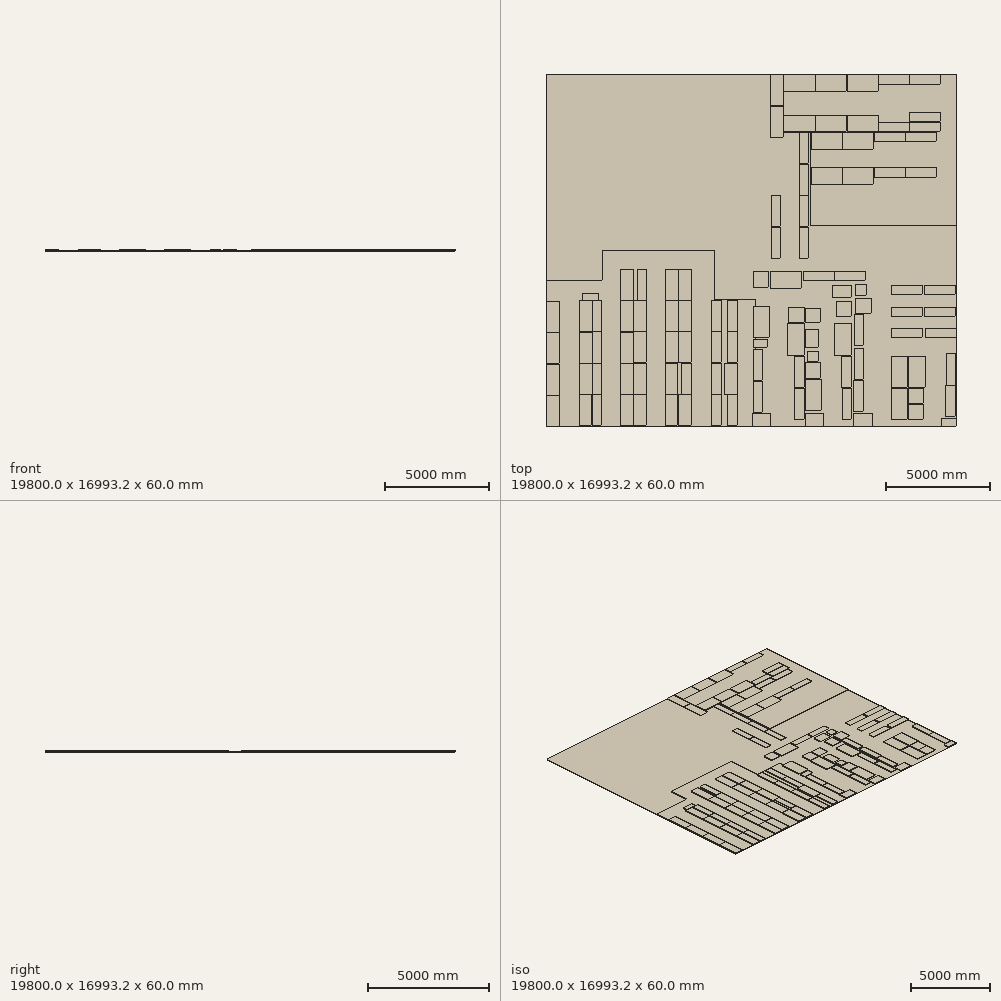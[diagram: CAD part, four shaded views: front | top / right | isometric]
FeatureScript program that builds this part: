
annotation { "Feature Type Name" : "Feature", "Feature Type Description" : "" }
export const myFeature = defineFeature(function(context is Context, id is Id, definition is map)
    precondition{}
    {
        {
            var Q0;
            Q0=qCreatedBy(makeId("Top.planeOp"),FACE);
            var sketch = newSketch(context, id + "F0", { "sketchPlane" : qUnion([Q0])});
            skLineSegment(sketch, "E0.bottom", {"start": v(9900, -8495) * mm, "end": v(-9900, -8495) * mm});
            skLineSegment(sketch, "E0.top", {"start": v(9900, 8495) * mm, "end": v(-9900, 8495) * mm});
            skLineSegment(sketch, "E0.left", {"start": v(9900, -8495) * mm, "end": v(9900, 8495) * mm});
            skLineSegment(sketch, "E0.right", {"start": v(-9900, -8495) * mm, "end": v(-9900, 8495) * mm});
            skPoint(sketch, "E0.middle", {"position": v(0, 0) * mm});
            skSolve(sketch);
        }
        {
            var Q0;
            Q0 = qSketchRegion(id + "F0", true);
            extrude(context, id + "F1", {"entities" : qUnion([Q0]), "depth" : 10 * mm});
        }
        {
            var Q0;
            Q0=makeQuery(id+"F1.opExtrude","CAP_FACE",FACE,{"disambiguationData":[OSD([sQuery(id+"F0.wireOp",EDGE,"E0.bottom"),sQuery(id+"F0.wireOp",EDGE,"E0.top"),sQuery(id+"F0.wireOp",EDGE,"E0.left"),sQuery(id+"F0.wireOp",EDGE,"E0.right")])],"isStart":false});
            var sketch = newSketch(context, id + "F2", { "sketchPlane" : qUnion([Q0])});
            skLineSegment(sketch, "E1", {"start": v(-9900, -8495) * mm, "end": v(-9900, -1435) * mm});
            skLineSegment(sketch, "E2", {"start": v(-9900, -1435) * mm, "end": v(-7200, -1435) * mm});
            skLineSegment(sketch, "E3", {"start": v(-7200, -1435) * mm, "end": v(-7200, -5) * mm});
            skLineSegment(sketch, "E4", {"start": v(-7200, -5) * mm, "end": v(-1800, -5) * mm});
            skLineSegment(sketch, "E5", {"start": v(-1800, -5) * mm, "end": v(-1800, -2355) * mm});
            skLineSegment(sketch, "E6", {"start": v(-1800, -2355) * mm, "end": v(200, -2355) * mm});
            skLineSegment(sketch, "E7", {"start": v(200, -2355) * mm, "end": v(200, -8495) * mm});
            skLineSegment(sketch, "E8", {"start": v(200, -8495) * mm, "end": v(-9900, -8495) * mm});
            skLineSegment(sketch, "E9", {"start": v(9900, 1195) * mm, "end": v(9900, 8495) * mm});
            skLineSegment(sketch, "E10", {"start": v(9900, 8495) * mm, "end": v(1550, 8495) * mm});
            skLineSegment(sketch, "E11", {"start": v(1550, 8495) * mm, "end": v(1550, 5715) * mm});
            skLineSegment(sketch, "E12", {"start": v(1550, 5715) * mm, "end": v(2850, 5715) * mm});
            skLineSegment(sketch, "E13", {"start": v(2850, 5715) * mm, "end": v(2850, 1195) * mm});
            skLineSegment(sketch, "E14", {"start": v(2850, 1195) * mm, "end": v(9900, 1195) * mm});
            skLineSegment(sketch, "E15.left", {"start": v(3458.32, 469.72) * mm, "end": v(3008.32, 469.72) * mm});
            skPoint(sketch, "E15.middle", {"position": v(3233.32, -280.28) * mm});
            skLineSegment(sketch, "E16.left", {"start": v(4716.05, -36.44) * mm, "end": v(4096.05, -36.44) * mm});
            skPoint(sketch, "E16.middle", {"position": v(4406.05, -786.44) * mm});
            skSolve(sketch);
        }
        {
            var Q0;
            Q0 = qSketchRegion(id + "F2", true);
            extrude(context, id + "F3", {"entities" : qUnion([Q0]), "operationType" : NewBodyOperationType.ADD, "depth" : 25 * mm});
        }
        {
            var Q0;
            Q0=makeQuery(id+"F3.opExtrude","CAP_FACE",FACE,{"disambiguationData":[OSD([sQuery(id+"F2.wireOp",EDGE,"E1"),sQuery(id+"F2.wireOp",EDGE,"E2"),sQuery(id+"F2.wireOp",EDGE,"E3"),sQuery(id+"F2.wireOp",EDGE,"E4"),sQuery(id+"F2.wireOp",EDGE,"E5"),sQuery(id+"F2.wireOp",EDGE,"E6"),sQuery(id+"F2.wireOp",EDGE,"E7"),sQuery(id+"F2.wireOp",EDGE,"E8")])],"isStart":false});
            var sketch = newSketch(context, id + "F4", { "sketchPlane" : qUnion([Q0])});
            skLineSegment(sketch, "E17.bottom", {"start": v(-9900, -8495) * mm, "end": v(-9900, -6995) * mm});
            skLineSegment(sketch, "E17.top", {"start": v(-9280, -8495) * mm, "end": v(-9280, -6995) * mm});
            skLineSegment(sketch, "E17.left", {"start": v(-9900, -8495) * mm, "end": v(-9280, -8495) * mm});
            skLineSegment(sketch, "E17.right", {"start": v(-9900, -6995) * mm, "end": v(-9280, -6995) * mm});
            skPoint(sketch, "E17.middle", {"position": v(-9590, -7745) * mm});
            skLineSegment(sketch, "E18.bottom", {"start": v(-9892.84, -6987.42) * mm, "end": v(-9892.84, -5487.42) * mm});
            skLineSegment(sketch, "E18.top", {"start": v(-9272.84, -6987.42) * mm, "end": v(-9272.84, -5487.42) * mm});
            skLineSegment(sketch, "E18.left", {"start": v(-9892.84, -6987.42) * mm, "end": v(-9272.84, -6987.42) * mm});
            skLineSegment(sketch, "E18.right", {"start": v(-9892.84, -5487.42) * mm, "end": v(-9272.84, -5487.42) * mm});
            skPoint(sketch, "E18.middle", {"position": v(-9582.84, -6237.42) * mm});
            skLineSegment(sketch, "E19.bottom", {"start": v(-9892.84, -5474.56) * mm, "end": v(-9892.84, -3974.56) * mm});
            skLineSegment(sketch, "E19.top", {"start": v(-9272.84, -5474.56) * mm, "end": v(-9272.84, -3974.56) * mm});
            skLineSegment(sketch, "E19.left", {"start": v(-9892.84, -5474.56) * mm, "end": v(-9272.84, -5474.56) * mm});
            skLineSegment(sketch, "E19.right", {"start": v(-9892.84, -3974.56) * mm, "end": v(-9272.84, -3974.56) * mm});
            skPoint(sketch, "E19.middle", {"position": v(-9582.84, -4724.56) * mm});
            skLineSegment(sketch, "E20.bottom", {"start": v(-9892.84, -3964.29) * mm, "end": v(-9892.84, -2464.29) * mm});
            skLineSegment(sketch, "E20.top", {"start": v(-9272.84, -3964.29) * mm, "end": v(-9272.84, -2464.29) * mm});
            skLineSegment(sketch, "E20.left", {"start": v(-9892.84, -3964.29) * mm, "end": v(-9272.84, -3964.29) * mm});
            skLineSegment(sketch, "E20.right", {"start": v(-9892.84, -2464.29) * mm, "end": v(-9272.84, -2464.29) * mm});
            skPoint(sketch, "E20.middle", {"position": v(-9582.84, -3214.29) * mm});
            skLineSegment(sketch, "E21.bottom", {"start": v(-8329.6, -8467.89) * mm, "end": v(-8329.6, -6967.89) * mm});
            skLineSegment(sketch, "E21.top", {"start": v(-7709.6, -8467.89) * mm, "end": v(-7709.6, -6967.89) * mm});
            skLineSegment(sketch, "E21.left", {"start": v(-8329.6, -8467.89) * mm, "end": v(-7709.6, -8467.89) * mm});
            skLineSegment(sketch, "E21.right", {"start": v(-8329.6, -6967.89) * mm, "end": v(-7709.6, -6967.89) * mm});
            skPoint(sketch, "E21.middle", {"position": v(-8019.6, -7717.89) * mm});
            skLineSegment(sketch, "E22.bottom", {"start": v(-8322.44, -6960.31) * mm, "end": v(-8322.44, -5460.31) * mm});
            skLineSegment(sketch, "E22.top", {"start": v(-7702.44, -6960.31) * mm, "end": v(-7702.44, -5460.31) * mm});
            skLineSegment(sketch, "E22.left", {"start": v(-8322.44, -6960.31) * mm, "end": v(-7702.44, -6960.31) * mm});
            skLineSegment(sketch, "E22.right", {"start": v(-8322.44, -5460.31) * mm, "end": v(-7702.44, -5460.31) * mm});
            skPoint(sketch, "E22.middle", {"position": v(-8012.44, -6210.31) * mm});
            skLineSegment(sketch, "E23.bottom", {"start": v(-8322.44, -5447.45) * mm, "end": v(-8322.44, -3947.45) * mm});
            skLineSegment(sketch, "E23.top", {"start": v(-7702.44, -5447.45) * mm, "end": v(-7702.44, -3947.45) * mm});
            skLineSegment(sketch, "E23.left", {"start": v(-8322.44, -5447.45) * mm, "end": v(-7702.44, -5447.45) * mm});
            skLineSegment(sketch, "E23.right", {"start": v(-8322.44, -3947.45) * mm, "end": v(-7702.44, -3947.45) * mm});
            skPoint(sketch, "E23.middle", {"position": v(-8012.44, -4697.45) * mm});
            skLineSegment(sketch, "E24.bottom", {"start": v(-8322.44, -3937.18) * mm, "end": v(-8322.44, -2437.18) * mm});
            skLineSegment(sketch, "E24.top", {"start": v(-7702.44, -3937.18) * mm, "end": v(-7702.44, -2437.18) * mm});
            skLineSegment(sketch, "E24.left", {"start": v(-8322.44, -3937.18) * mm, "end": v(-7702.44, -3937.18) * mm});
            skLineSegment(sketch, "E24.right", {"start": v(-8322.44, -2437.18) * mm, "end": v(-7702.44, -2437.18) * mm});
            skPoint(sketch, "E24.middle", {"position": v(-8012.44, -3187.18) * mm});
            skLineSegment(sketch, "E25.bottom", {"start": v(-7690, -8467.89) * mm, "end": v(-7690, -6967.89) * mm});
            skLineSegment(sketch, "E25.top", {"start": v(-7240, -8467.89) * mm, "end": v(-7240, -6967.89) * mm});
            skLineSegment(sketch, "E25.left", {"start": v(-7690, -8467.89) * mm, "end": v(-7240, -8467.89) * mm});
            skLineSegment(sketch, "E25.right", {"start": v(-7690, -6967.89) * mm, "end": v(-7240, -6967.89) * mm});
            skPoint(sketch, "E25.middle", {"position": v(-7465, -7717.89) * mm});
            skLineSegment(sketch, "E26.bottom", {"start": v(-7690, -6949.05) * mm, "end": v(-7690, -5449.05) * mm});
            skLineSegment(sketch, "E26.top", {"start": v(-7240, -6949.05) * mm, "end": v(-7240, -5449.05) * mm});
            skLineSegment(sketch, "E26.left", {"start": v(-7690, -6949.05) * mm, "end": v(-7240, -6949.05) * mm});
            skLineSegment(sketch, "E26.right", {"start": v(-7690, -5449.05) * mm, "end": v(-7240, -5449.05) * mm});
            skPoint(sketch, "E26.middle", {"position": v(-7465, -6199.05) * mm});
            skLineSegment(sketch, "E27.bottom", {"start": v(-7690, -5437.57) * mm, "end": v(-7690, -3937.57) * mm});
            skLineSegment(sketch, "E27.top", {"start": v(-7240, -5437.57) * mm, "end": v(-7240, -3937.57) * mm});
            skLineSegment(sketch, "E27.left", {"start": v(-7690, -5437.57) * mm, "end": v(-7240, -5437.57) * mm});
            skLineSegment(sketch, "E27.right", {"start": v(-7690, -3937.57) * mm, "end": v(-7240, -3937.57) * mm});
            skPoint(sketch, "E27.middle", {"position": v(-7465, -4687.57) * mm});
            skLineSegment(sketch, "E28.bottom", {"start": v(-7690, -3928.07) * mm, "end": v(-7690, -2428.07) * mm});
            skLineSegment(sketch, "E28.top", {"start": v(-7240, -3928.07) * mm, "end": v(-7240, -2428.07) * mm});
            skLineSegment(sketch, "E28.left", {"start": v(-7690, -3928.07) * mm, "end": v(-7240, -3928.07) * mm});
            skLineSegment(sketch, "E28.right", {"start": v(-7690, -2428.07) * mm, "end": v(-7240, -2428.07) * mm});
            skPoint(sketch, "E28.middle", {"position": v(-7465, -3178.07) * mm});
            skLineSegment(sketch, "E29.bottom", {"start": v(-8177.13, -2054.5) * mm, "end": v(-7388.6, -2054.5) * mm});
            skLineSegment(sketch, "E29.top", {"start": v(-8177.13, -2400.4) * mm, "end": v(-7388.6, -2400.4) * mm});
            skLineSegment(sketch, "E29.left", {"start": v(-8177.13, -2054.5) * mm, "end": v(-8177.13, -2400.4) * mm});
            skLineSegment(sketch, "E29.right", {"start": v(-7388.6, -2054.5) * mm, "end": v(-7388.6, -2400.4) * mm});
            skLineSegment(sketch, "E30.bottom", {"start": v(-6340, -8467.89) * mm, "end": v(-6340, -6967.89) * mm});
            skLineSegment(sketch, "E30.top", {"start": v(-5720, -8467.89) * mm, "end": v(-5720, -6967.89) * mm});
            skLineSegment(sketch, "E30.left", {"start": v(-6340, -8467.89) * mm, "end": v(-5720, -8467.89) * mm});
            skLineSegment(sketch, "E30.right", {"start": v(-6340, -6967.89) * mm, "end": v(-5720, -6967.89) * mm});
            skPoint(sketch, "E30.middle", {"position": v(-6030, -7717.89) * mm});
            skLineSegment(sketch, "E31.bottom", {"start": v(-6340, -6949.05) * mm, "end": v(-6340, -5449.05) * mm});
            skLineSegment(sketch, "E31.top", {"start": v(-5720, -6949.05) * mm, "end": v(-5720, -5449.05) * mm});
            skLineSegment(sketch, "E31.left", {"start": v(-6340, -6949.05) * mm, "end": v(-5720, -6949.05) * mm});
            skLineSegment(sketch, "E31.right", {"start": v(-6340, -5449.05) * mm, "end": v(-5720, -5449.05) * mm});
            skPoint(sketch, "E31.middle", {"position": v(-6030, -6199.05) * mm});
            skLineSegment(sketch, "E32.bottom", {"start": v(-6332.83, -5441.47) * mm, "end": v(-6332.83, -3941.47) * mm});
            skLineSegment(sketch, "E32.top", {"start": v(-5712.83, -5441.47) * mm, "end": v(-5712.83, -3941.47) * mm});
            skLineSegment(sketch, "E32.left", {"start": v(-6332.83, -5441.47) * mm, "end": v(-5712.83, -5441.47) * mm});
            skLineSegment(sketch, "E32.right", {"start": v(-6332.83, -3941.47) * mm, "end": v(-5712.83, -3941.47) * mm});
            skPoint(sketch, "E32.middle", {"position": v(-6022.83, -4691.47) * mm});
            skLineSegment(sketch, "E33.bottom", {"start": v(-6332.83, -3928.6) * mm, "end": v(-6332.83, -2428.6) * mm});
            skLineSegment(sketch, "E33.top", {"start": v(-5712.83, -3928.6) * mm, "end": v(-5712.83, -2428.6) * mm});
            skLineSegment(sketch, "E33.left", {"start": v(-6332.83, -3928.6) * mm, "end": v(-5712.83, -3928.6) * mm});
            skLineSegment(sketch, "E33.right", {"start": v(-6332.83, -2428.6) * mm, "end": v(-5712.83, -2428.6) * mm});
            skPoint(sketch, "E33.middle", {"position": v(-6022.83, -3178.6) * mm});
            skLineSegment(sketch, "E34.bottom", {"start": v(-6332.83, -2418.34) * mm, "end": v(-6332.83, -918.34) * mm});
            skLineSegment(sketch, "E34.top", {"start": v(-5712.83, -2418.34) * mm, "end": v(-5712.83, -918.34) * mm});
            skLineSegment(sketch, "E34.left", {"start": v(-6332.83, -2418.34) * mm, "end": v(-5712.83, -2418.34) * mm});
            skLineSegment(sketch, "E34.right", {"start": v(-6332.83, -918.34) * mm, "end": v(-5712.83, -918.34) * mm});
            skPoint(sketch, "E34.middle", {"position": v(-6022.83, -1668.34) * mm});
            skLineSegment(sketch, "E35.bottom", {"start": v(-5694.35, -8456.4) * mm, "end": v(-5694.35, -6956.4) * mm});
            skLineSegment(sketch, "E35.top", {"start": v(-5074.35, -8456.4) * mm, "end": v(-5074.35, -6956.4) * mm});
            skLineSegment(sketch, "E35.left", {"start": v(-5694.35, -8456.4) * mm, "end": v(-5074.35, -8456.4) * mm});
            skLineSegment(sketch, "E35.right", {"start": v(-5694.35, -6956.4) * mm, "end": v(-5074.35, -6956.4) * mm});
            skPoint(sketch, "E35.middle", {"position": v(-5384.35, -7706.4) * mm});
            skLineSegment(sketch, "E36.bottom", {"start": v(-5694.35, -6937.55) * mm, "end": v(-5694.35, -5437.55) * mm});
            skLineSegment(sketch, "E36.top", {"start": v(-5074.35, -6937.55) * mm, "end": v(-5074.35, -5437.55) * mm});
            skLineSegment(sketch, "E36.left", {"start": v(-5694.35, -6937.55) * mm, "end": v(-5074.35, -6937.55) * mm});
            skLineSegment(sketch, "E36.right", {"start": v(-5694.35, -5437.55) * mm, "end": v(-5074.35, -5437.55) * mm});
            skPoint(sketch, "E36.middle", {"position": v(-5384.35, -6187.55) * mm});
            skLineSegment(sketch, "E37.bottom", {"start": v(-5687.2, -5429.97) * mm, "end": v(-5687.2, -3929.97) * mm});
            skLineSegment(sketch, "E37.top", {"start": v(-5067.2, -5429.97) * mm, "end": v(-5067.2, -3929.97) * mm});
            skLineSegment(sketch, "E37.left", {"start": v(-5687.2, -5429.97) * mm, "end": v(-5067.2, -5429.97) * mm});
            skLineSegment(sketch, "E37.right", {"start": v(-5687.2, -3929.97) * mm, "end": v(-5067.2, -3929.97) * mm});
            skPoint(sketch, "E37.middle", {"position": v(-5377.2, -4679.97) * mm});
            skLineSegment(sketch, "E38.bottom", {"start": v(-5687.2, -3917.11) * mm, "end": v(-5687.2, -2417.11) * mm});
            skLineSegment(sketch, "E38.top", {"start": v(-5067.2, -3917.11) * mm, "end": v(-5067.2, -2417.11) * mm});
            skLineSegment(sketch, "E38.left", {"start": v(-5687.2, -3917.11) * mm, "end": v(-5067.2, -3917.11) * mm});
            skLineSegment(sketch, "E38.right", {"start": v(-5687.2, -2417.11) * mm, "end": v(-5067.2, -2417.11) * mm});
            skPoint(sketch, "E38.middle", {"position": v(-5377.2, -3167.11) * mm});
            skPoint(sketch, "E39.middle", {"position": v(-5377.2, -1656.84) * mm});
            skLineSegment(sketch, "E40.bottom", {"start": v(-5518.6, -2401.56) * mm, "end": v(-5518.6, -901.56) * mm});
            skLineSegment(sketch, "E40.top", {"start": v(-5068.6, -2401.56) * mm, "end": v(-5068.6, -901.56) * mm});
            skLineSegment(sketch, "E40.left", {"start": v(-5518.6, -2401.56) * mm, "end": v(-5068.6, -2401.56) * mm});
            skLineSegment(sketch, "E40.right", {"start": v(-5518.6, -901.56) * mm, "end": v(-5068.6, -901.56) * mm});
            skPoint(sketch, "E40.middle", {"position": v(-5293.6, -1651.56) * mm});
            skLineSegment(sketch, "E41.bottom", {"start": v(-4174.35, -8456.4) * mm, "end": v(-4174.35, -6956.4) * mm});
            skLineSegment(sketch, "E41.top", {"start": v(-3554.35, -8456.4) * mm, "end": v(-3554.35, -6956.4) * mm});
            skLineSegment(sketch, "E41.left", {"start": v(-4174.35, -8456.4) * mm, "end": v(-3554.35, -8456.4) * mm});
            skLineSegment(sketch, "E41.right", {"start": v(-4174.35, -6956.4) * mm, "end": v(-3554.35, -6956.4) * mm});
            skPoint(sketch, "E41.middle", {"position": v(-3864.35, -7706.4) * mm});
            skLineSegment(sketch, "E42.bottom", {"start": v(-4170.79, -6937.55) * mm, "end": v(-4170.79, -5437.55) * mm});
            skLineSegment(sketch, "E42.top", {"start": v(-3550.79, -6937.55) * mm, "end": v(-3550.79, -5437.55) * mm});
            skLineSegment(sketch, "E42.left", {"start": v(-4170.79, -6937.55) * mm, "end": v(-3550.79, -6937.55) * mm});
            skLineSegment(sketch, "E42.right", {"start": v(-4170.79, -5437.55) * mm, "end": v(-3550.79, -5437.55) * mm});
            skPoint(sketch, "E42.middle", {"position": v(-3860.79, -6187.55) * mm});
            skLineSegment(sketch, "E43.bottom", {"start": v(-4163.63, -5429.97) * mm, "end": v(-4163.63, -3929.97) * mm});
            skLineSegment(sketch, "E43.top", {"start": v(-3543.63, -5429.97) * mm, "end": v(-3543.63, -3929.97) * mm});
            skLineSegment(sketch, "E43.left", {"start": v(-4163.63, -5429.97) * mm, "end": v(-3543.63, -5429.97) * mm});
            skLineSegment(sketch, "E43.right", {"start": v(-4163.63, -3929.97) * mm, "end": v(-3543.63, -3929.97) * mm});
            skPoint(sketch, "E43.middle", {"position": v(-3853.63, -4679.97) * mm});
            skLineSegment(sketch, "E44.bottom", {"start": v(-4163.63, -3917.11) * mm, "end": v(-4163.63, -2417.11) * mm});
            skLineSegment(sketch, "E44.top", {"start": v(-3543.63, -3917.11) * mm, "end": v(-3543.63, -2417.11) * mm});
            skLineSegment(sketch, "E44.left", {"start": v(-4163.63, -3917.11) * mm, "end": v(-3543.63, -3917.11) * mm});
            skLineSegment(sketch, "E44.right", {"start": v(-4163.63, -2417.11) * mm, "end": v(-3543.63, -2417.11) * mm});
            skPoint(sketch, "E44.middle", {"position": v(-3853.63, -3167.11) * mm});
            skLineSegment(sketch, "E45.bottom", {"start": v(-4163.63, -2406.84) * mm, "end": v(-4163.63, -906.84) * mm});
            skLineSegment(sketch, "E45.top", {"start": v(-3543.63, -2406.84) * mm, "end": v(-3543.63, -906.84) * mm});
            skLineSegment(sketch, "E45.left", {"start": v(-4163.63, -2406.84) * mm, "end": v(-3543.63, -2406.84) * mm});
            skLineSegment(sketch, "E45.right", {"start": v(-4163.63, -906.84) * mm, "end": v(-3543.63, -906.84) * mm});
            skPoint(sketch, "E45.middle", {"position": v(-3853.63, -1656.84) * mm});
            skLineSegment(sketch, "E46.bottom", {"start": v(-3527.86, -8456.8) * mm, "end": v(-3527.86, -6956.8) * mm});
            skLineSegment(sketch, "E46.top", {"start": v(-2907.86, -8456.8) * mm, "end": v(-2907.86, -6956.8) * mm});
            skLineSegment(sketch, "E46.left", {"start": v(-3527.86, -8456.8) * mm, "end": v(-2907.86, -8456.8) * mm});
            skLineSegment(sketch, "E46.right", {"start": v(-3527.86, -6956.8) * mm, "end": v(-2907.86, -6956.8) * mm});
            skPoint(sketch, "E46.middle", {"position": v(-3217.86, -7706.8) * mm});
            skPoint(sketch, "E47.middle", {"position": v(-3214.3, -6187.96) * mm});
            skLineSegment(sketch, "E48.bottom", {"start": v(-3517.14, -5430.38) * mm, "end": v(-3517.14, -3930.38) * mm});
            skLineSegment(sketch, "E48.top", {"start": v(-2897.14, -5430.38) * mm, "end": v(-2897.14, -3930.38) * mm});
            skLineSegment(sketch, "E48.left", {"start": v(-3517.14, -5430.38) * mm, "end": v(-2897.14, -5430.38) * mm});
            skLineSegment(sketch, "E48.right", {"start": v(-3517.14, -3930.38) * mm, "end": v(-2897.14, -3930.38) * mm});
            skPoint(sketch, "E48.middle", {"position": v(-3207.14, -4680.38) * mm});
            skLineSegment(sketch, "E49.bottom", {"start": v(-3517.14, -3917.52) * mm, "end": v(-3517.14, -2417.52) * mm});
            skLineSegment(sketch, "E49.top", {"start": v(-2897.14, -3917.52) * mm, "end": v(-2897.14, -2417.52) * mm});
            skLineSegment(sketch, "E49.left", {"start": v(-3517.14, -3917.52) * mm, "end": v(-2897.14, -3917.52) * mm});
            skLineSegment(sketch, "E49.right", {"start": v(-3517.14, -2417.52) * mm, "end": v(-2897.14, -2417.52) * mm});
            skPoint(sketch, "E49.middle", {"position": v(-3207.14, -3167.52) * mm});
            skLineSegment(sketch, "E50.bottom", {"start": v(-3517.14, -2407.25) * mm, "end": v(-3517.14, -907.25) * mm});
            skLineSegment(sketch, "E50.top", {"start": v(-2897.14, -2407.25) * mm, "end": v(-2897.14, -907.25) * mm});
            skLineSegment(sketch, "E50.left", {"start": v(-3517.14, -2407.25) * mm, "end": v(-2897.14, -2407.25) * mm});
            skLineSegment(sketch, "E50.right", {"start": v(-3517.14, -907.25) * mm, "end": v(-2897.14, -907.25) * mm});
            skPoint(sketch, "E50.middle", {"position": v(-3207.14, -1657.25) * mm});
            skLineSegment(sketch, "E51.bottom", {"start": v(-3359.83, -6937.55) * mm, "end": v(-3359.83, -5437.55) * mm});
            skLineSegment(sketch, "E51.top", {"start": v(-2909.83, -6937.55) * mm, "end": v(-2909.83, -5437.55) * mm});
            skLineSegment(sketch, "E51.left", {"start": v(-3359.83, -6937.55) * mm, "end": v(-2909.83, -6937.55) * mm});
            skLineSegment(sketch, "E51.right", {"start": v(-3359.83, -5437.55) * mm, "end": v(-2909.83, -5437.55) * mm});
            skPoint(sketch, "E51.middle", {"position": v(-3134.83, -6187.55) * mm});
            skLineSegment(sketch, "E52.bottom", {"start": v(-1907.64, -8456.4) * mm, "end": v(-1907.64, -6956.4) * mm});
            skLineSegment(sketch, "E52.top", {"start": v(-1457.64, -8456.4) * mm, "end": v(-1457.64, -6956.4) * mm});
            skLineSegment(sketch, "E52.left", {"start": v(-1907.64, -8456.4) * mm, "end": v(-1457.64, -8456.4) * mm});
            skLineSegment(sketch, "E52.right", {"start": v(-1907.64, -6956.4) * mm, "end": v(-1457.64, -6956.4) * mm});
            skPoint(sketch, "E52.middle", {"position": v(-1682.64, -7706.4) * mm});
            skLineSegment(sketch, "E53.bottom", {"start": v(-1907.64, -6937.55) * mm, "end": v(-1907.64, -5437.55) * mm});
            skLineSegment(sketch, "E53.top", {"start": v(-1457.64, -6937.55) * mm, "end": v(-1457.64, -5437.55) * mm});
            skLineSegment(sketch, "E53.left", {"start": v(-1907.64, -6937.55) * mm, "end": v(-1457.64, -6937.55) * mm});
            skLineSegment(sketch, "E53.right", {"start": v(-1907.64, -5437.55) * mm, "end": v(-1457.64, -5437.55) * mm});
            skPoint(sketch, "E53.middle", {"position": v(-1682.64, -6187.55) * mm});
            skLineSegment(sketch, "E54.bottom", {"start": v(-1907.64, -5429.98) * mm, "end": v(-1907.64, -3929.98) * mm});
            skLineSegment(sketch, "E54.top", {"start": v(-1457.64, -5429.98) * mm, "end": v(-1457.64, -3929.98) * mm});
            skLineSegment(sketch, "E54.left", {"start": v(-1907.64, -5429.98) * mm, "end": v(-1457.64, -5429.98) * mm});
            skLineSegment(sketch, "E54.right", {"start": v(-1907.64, -3929.98) * mm, "end": v(-1457.64, -3929.98) * mm});
            skPoint(sketch, "E54.middle", {"position": v(-1682.64, -4679.98) * mm});
            skLineSegment(sketch, "E55.bottom", {"start": v(-1907.64, -3917.11) * mm, "end": v(-1907.64, -2417.11) * mm});
            skLineSegment(sketch, "E55.top", {"start": v(-1457.64, -3917.11) * mm, "end": v(-1457.64, -2417.11) * mm});
            skLineSegment(sketch, "E55.left", {"start": v(-1907.64, -3917.11) * mm, "end": v(-1457.64, -3917.11) * mm});
            skLineSegment(sketch, "E55.right", {"start": v(-1907.64, -2417.11) * mm, "end": v(-1457.64, -2417.11) * mm});
            skPoint(sketch, "E55.middle", {"position": v(-1682.64, -3167.11) * mm});
            skLineSegment(sketch, "E56.bottom", {"start": v(-1149.63, -8456.4) * mm, "end": v(-1149.63, -6956.4) * mm});
            skLineSegment(sketch, "E56.top", {"start": v(-699.63, -8456.4) * mm, "end": v(-699.63, -6956.4) * mm});
            skLineSegment(sketch, "E56.left", {"start": v(-1149.63, -8456.4) * mm, "end": v(-699.63, -8456.4) * mm});
            skLineSegment(sketch, "E56.right", {"start": v(-1149.63, -6956.4) * mm, "end": v(-699.63, -6956.4) * mm});
            skPoint(sketch, "E56.middle", {"position": v(-924.63, -7706.4) * mm});
            skLineSegment(sketch, "E57.bottom", {"start": v(-1318.62, -6937.55) * mm, "end": v(-1318.62, -5437.55) * mm});
            skLineSegment(sketch, "E57.top", {"start": v(-698.62, -6937.55) * mm, "end": v(-698.62, -5437.55) * mm});
            skLineSegment(sketch, "E57.left", {"start": v(-1318.62, -6937.55) * mm, "end": v(-698.62, -6937.55) * mm});
            skPoint(sketch, "E57.middle", {"position": v(-1008.62, -6187.55) * mm});
            skLineSegment(sketch, "E58", {"start": v(-1318.62, -5437.55) * mm, "end": v(-698.62, -5437.55) * mm});
            skLineSegment(sketch, "E59.right", {"start": v(-1149.63, -5429.98) * mm, "end": v(-699.63, -5429.98) * mm});
            skLineSegment(sketch, "E60.bottom", {"start": v(-1149.63, -5422.4) * mm, "end": v(-1149.63, -3922.4) * mm});
            skLineSegment(sketch, "E60.top", {"start": v(-699.63, -5422.4) * mm, "end": v(-699.63, -3922.4) * mm});
            skLineSegment(sketch, "E60.left", {"start": v(-1149.63, -5422.4) * mm, "end": v(-699.63, -5422.4) * mm});
            skLineSegment(sketch, "E60.right", {"start": v(-1149.63, -3922.4) * mm, "end": v(-699.63, -3922.4) * mm});
            skPoint(sketch, "E60.middle", {"position": v(-924.63, -4672.4) * mm});
            skLineSegment(sketch, "E61.bottom", {"start": v(-1149.63, -3909.54) * mm, "end": v(-1149.63, -2409.54) * mm});
            skLineSegment(sketch, "E61.top", {"start": v(-699.63, -3909.54) * mm, "end": v(-699.63, -2409.54) * mm});
            skLineSegment(sketch, "E61.left", {"start": v(-1149.63, -3909.54) * mm, "end": v(-699.63, -3909.54) * mm});
            skLineSegment(sketch, "E61.right", {"start": v(-1149.63, -2409.54) * mm, "end": v(-699.63, -2409.54) * mm});
            skPoint(sketch, "E61.middle", {"position": v(-924.63, -3159.54) * mm});
            skLineSegment(sketch, "E62.bottom", {"start": v(1567.77, 8486.8) * mm, "end": v(3067.77, 8486.8) * mm});
            skLineSegment(sketch, "E62.top", {"start": v(1567.77, 7686.8) * mm, "end": v(3067.77, 7686.8) * mm});
            skLineSegment(sketch, "E62.left", {"start": v(1567.77, 8486.8) * mm, "end": v(1567.77, 7686.8) * mm});
            skLineSegment(sketch, "E62.right", {"start": v(3067.77, 8486.8) * mm, "end": v(3067.77, 7686.8) * mm});
            skLineSegment(sketch, "E63.bottom", {"start": v(3090.19, 8486.8) * mm, "end": v(4590.19, 8486.8) * mm});
            skLineSegment(sketch, "E63.top", {"start": v(3090.19, 7686.8) * mm, "end": v(4590.19, 7686.8) * mm});
            skLineSegment(sketch, "E63.left", {"start": v(3090.19, 8486.8) * mm, "end": v(3090.19, 7686.8) * mm});
            skLineSegment(sketch, "E63.right", {"start": v(4590.19, 8486.8) * mm, "end": v(4590.19, 7686.8) * mm});
            skLineSegment(sketch, "E64.bottom", {"start": v(4613.3, 8486.8) * mm, "end": v(6113.3, 8486.8) * mm});
            skLineSegment(sketch, "E64.top", {"start": v(4613.3, 7686.8) * mm, "end": v(6113.3, 7686.8) * mm});
            skLineSegment(sketch, "E64.left", {"start": v(4613.3, 8486.8) * mm, "end": v(4613.3, 7686.8) * mm});
            skLineSegment(sketch, "E64.right", {"start": v(6113.3, 8486.8) * mm, "end": v(6113.3, 7686.8) * mm});
            skLineSegment(sketch, "E65.bottom", {"start": v(6130.67, 8482.3) * mm, "end": v(7630.67, 8482.3) * mm});
            skLineSegment(sketch, "E65.top", {"start": v(6130.67, 8032.3) * mm, "end": v(7630.67, 8032.3) * mm});
            skLineSegment(sketch, "E65.left", {"start": v(6130.67, 8482.3) * mm, "end": v(6130.67, 8032.3) * mm});
            skLineSegment(sketch, "E65.right", {"start": v(7630.67, 8482.3) * mm, "end": v(7630.67, 8032.3) * mm});
            skPoint(sketch, "E65.middle", {"position": v(6880.67, 8257.3) * mm});
            skLineSegment(sketch, "E66.bottom", {"start": v(7648.58, 8482.3) * mm, "end": v(9148.58, 8482.3) * mm});
            skLineSegment(sketch, "E66.top", {"start": v(7648.58, 8032.3) * mm, "end": v(9148.58, 8032.3) * mm});
            skLineSegment(sketch, "E66.left", {"start": v(7648.58, 8482.3) * mm, "end": v(7648.58, 8032.3) * mm});
            skLineSegment(sketch, "E66.right", {"start": v(9148.58, 8482.3) * mm, "end": v(9148.58, 8032.3) * mm});
            skPoint(sketch, "E66.middle", {"position": v(8398.58, 8257.3) * mm});
            skLineSegment(sketch, "E67.bottom", {"start": v(1567.77, 6539.26) * mm, "end": v(3067.77, 6539.26) * mm});
            skLineSegment(sketch, "E67.top", {"start": v(1567.77, 5739.26) * mm, "end": v(3067.77, 5739.26) * mm});
            skLineSegment(sketch, "E67.left", {"start": v(1567.77, 6539.26) * mm, "end": v(1567.77, 5739.26) * mm});
            skLineSegment(sketch, "E67.right", {"start": v(3067.77, 6539.26) * mm, "end": v(3067.77, 5739.26) * mm});
            skLineSegment(sketch, "E68.bottom", {"start": v(3090.19, 6539.26) * mm, "end": v(4590.19, 6539.26) * mm});
            skLineSegment(sketch, "E68.top", {"start": v(3090.19, 5739.26) * mm, "end": v(4590.19, 5739.26) * mm});
            skLineSegment(sketch, "E68.left", {"start": v(3090.19, 6539.26) * mm, "end": v(3090.19, 5739.26) * mm});
            skLineSegment(sketch, "E68.right", {"start": v(4590.19, 6539.26) * mm, "end": v(4590.19, 5739.26) * mm});
            skLineSegment(sketch, "E69.bottom", {"start": v(4613.3, 6539.26) * mm, "end": v(6113.3, 6539.26) * mm});
            skLineSegment(sketch, "E69.top", {"start": v(4613.3, 5739.26) * mm, "end": v(6113.3, 5739.26) * mm});
            skLineSegment(sketch, "E69.left", {"start": v(4613.3, 6539.26) * mm, "end": v(4613.3, 5739.26) * mm});
            skLineSegment(sketch, "E69.right", {"start": v(6113.3, 6539.26) * mm, "end": v(6113.3, 5739.26) * mm});
            skLineSegment(sketch, "E70.bottom", {"start": v(6130.67, 6189.26) * mm, "end": v(7630.67, 6189.26) * mm});
            skLineSegment(sketch, "E70.top", {"start": v(6130.67, 5739.26) * mm, "end": v(7630.67, 5739.26) * mm});
            skLineSegment(sketch, "E70.left", {"start": v(6130.67, 6189.26) * mm, "end": v(6130.67, 5739.26) * mm});
            skLineSegment(sketch, "E70.right", {"start": v(7630.67, 6189.26) * mm, "end": v(7630.67, 5739.26) * mm});
            skPoint(sketch, "E70.middle", {"position": v(6880.67, 5964.26) * mm});
            skLineSegment(sketch, "E71.bottom", {"start": v(7648.58, 6189.26) * mm, "end": v(9148.58, 6189.26) * mm});
            skLineSegment(sketch, "E71.top", {"start": v(7648.58, 5739.26) * mm, "end": v(9148.58, 5739.26) * mm});
            skLineSegment(sketch, "E71.left", {"start": v(7648.58, 6189.26) * mm, "end": v(7648.58, 5739.26) * mm});
            skLineSegment(sketch, "E71.right", {"start": v(9148.58, 6189.26) * mm, "end": v(9148.58, 5739.26) * mm});
            skPoint(sketch, "E71.middle", {"position": v(8398.58, 5964.26) * mm});
            skLineSegment(sketch, "E72.bottom", {"start": v(7648.58, 6659) * mm, "end": v(9148.58, 6659) * mm});
            skLineSegment(sketch, "E72.top", {"start": v(7648.58, 6209) * mm, "end": v(9148.58, 6209) * mm});
            skLineSegment(sketch, "E72.left", {"start": v(7648.58, 6659) * mm, "end": v(7648.58, 6209) * mm});
            skLineSegment(sketch, "E72.right", {"start": v(9148.58, 6659) * mm, "end": v(9148.58, 6209) * mm});
            skPoint(sketch, "E72.middle", {"position": v(8398.58, 6434) * mm});
            skLineSegment(sketch, "E73.bottom", {"start": v(2879.26, 5691.5) * mm, "end": v(4379.26, 5691.5) * mm});
            skLineSegment(sketch, "E73.top", {"start": v(2879.26, 4891.5) * mm, "end": v(4379.26, 4891.5) * mm});
            skLineSegment(sketch, "E73.left", {"start": v(2879.26, 5691.5) * mm, "end": v(2879.26, 4891.5) * mm});
            skLineSegment(sketch, "E73.right", {"start": v(4379.26, 5691.5) * mm, "end": v(4379.26, 4891.5) * mm});
            skLineSegment(sketch, "E74.bottom", {"start": v(4401.26, 5691.5) * mm, "end": v(5901.26, 5691.5) * mm});
            skLineSegment(sketch, "E74.top", {"start": v(4401.26, 4891.5) * mm, "end": v(5901.26, 4891.5) * mm});
            skLineSegment(sketch, "E74.left", {"start": v(4401.26, 5691.5) * mm, "end": v(4401.26, 4891.5) * mm});
            skLineSegment(sketch, "E74.right", {"start": v(5901.26, 5691.5) * mm, "end": v(5901.26, 4891.5) * mm});
            skLineSegment(sketch, "E75.bottom", {"start": v(5916.26, 5692.01) * mm, "end": v(7416.26, 5692.01) * mm});
            skLineSegment(sketch, "E75.top", {"start": v(5916.26, 5242.01) * mm, "end": v(7416.26, 5242.01) * mm});
            skLineSegment(sketch, "E75.left", {"start": v(5916.26, 5692.01) * mm, "end": v(5916.26, 5242.01) * mm});
            skLineSegment(sketch, "E75.right", {"start": v(7416.26, 5692.01) * mm, "end": v(7416.26, 5242.01) * mm});
            skPoint(sketch, "E75.middle", {"position": v(6666.26, 5467.01) * mm});
            skLineSegment(sketch, "E76.bottom", {"start": v(7444.13, 5692.01) * mm, "end": v(8944.13, 5692.01) * mm});
            skLineSegment(sketch, "E76.top", {"start": v(7444.13, 5242.01) * mm, "end": v(8944.13, 5242.01) * mm});
            skLineSegment(sketch, "E76.left", {"start": v(7444.13, 5692.01) * mm, "end": v(7444.13, 5242.01) * mm});
            skLineSegment(sketch, "E76.right", {"start": v(8944.13, 5692.01) * mm, "end": v(8944.13, 5242.01) * mm});
            skPoint(sketch, "E76.middle", {"position": v(8194.13, 5467.01) * mm});
            skLineSegment(sketch, "E77.bottom", {"start": v(7444.13, 3991.78) * mm, "end": v(8944.13, 3991.78) * mm});
            skLineSegment(sketch, "E77.top", {"start": v(7444.13, 3541.78) * mm, "end": v(8944.13, 3541.78) * mm});
            skLineSegment(sketch, "E77.left", {"start": v(7444.13, 3991.78) * mm, "end": v(7444.13, 3541.78) * mm});
            skLineSegment(sketch, "E77.right", {"start": v(8944.13, 3991.78) * mm, "end": v(8944.13, 3541.78) * mm});
            skPoint(sketch, "E77.middle", {"position": v(8194.13, 3766.78) * mm});
            skLineSegment(sketch, "E78.left", {"start": v(5901.26, 3992.32) * mm, "end": v(5901.26, 3542.32) * mm});
            skPoint(sketch, "E78.middle", {"position": v(6651.26, 3767.32) * mm});
            skLineSegment(sketch, "E79.bottom", {"start": v(4401.26, 3993.15) * mm, "end": v(5901.26, 3993.15) * mm});
            skLineSegment(sketch, "E79.top", {"start": v(4401.26, 3193.15) * mm, "end": v(5901.26, 3193.15) * mm});
            skLineSegment(sketch, "E79.left", {"start": v(4401.26, 3993.15) * mm, "end": v(4401.26, 3193.15) * mm});
            skLineSegment(sketch, "E79.right", {"start": v(5901.26, 3993.15) * mm, "end": v(5901.26, 3193.15) * mm});
            skLineSegment(sketch, "E80.bottom", {"start": v(2876.2, 3993.15) * mm, "end": v(4376.2, 3993.15) * mm});
            skLineSegment(sketch, "E80.top", {"start": v(2876.2, 3193.15) * mm, "end": v(4376.2, 3193.15) * mm});
            skLineSegment(sketch, "E80.left", {"start": v(2876.2, 3993.15) * mm, "end": v(2876.2, 3193.15) * mm});
            skLineSegment(sketch, "E80.right", {"start": v(4376.2, 3993.15) * mm, "end": v(4376.2, 3193.15) * mm});
            skLineSegment(sketch, "E81.bottom", {"start": v(5920.9, 3992.32) * mm, "end": v(7420.9, 3992.32) * mm});
            skLineSegment(sketch, "E81.top", {"start": v(5920.9, 3542.32) * mm, "end": v(7420.9, 3542.32) * mm});
            skLineSegment(sketch, "E81.left", {"start": v(5920.9, 3992.32) * mm, "end": v(5920.9, 3542.32) * mm});
            skLineSegment(sketch, "E81.right", {"start": v(7420.9, 3992.32) * mm, "end": v(7420.9, 3542.32) * mm});
            skPoint(sketch, "E81.middle", {"position": v(6670.9, 3767.32) * mm});
            skLineSegment(sketch, "E82.bottom", {"start": v(2750.27, 5676.61) * mm, "end": v(2750.27, 4176.61) * mm});
            skLineSegment(sketch, "E82.top", {"start": v(2300.27, 5676.61) * mm, "end": v(2300.27, 4176.61) * mm});
            skLineSegment(sketch, "E82.left", {"start": v(2750.27, 5676.61) * mm, "end": v(2300.27, 5676.61) * mm});
            skLineSegment(sketch, "E82.right", {"start": v(2750.27, 4176.61) * mm, "end": v(2300.27, 4176.61) * mm});
            skPoint(sketch, "E82.middle", {"position": v(2525.27, 4926.61) * mm});
            skLineSegment(sketch, "E83.bottom", {"start": v(2750.27, 4155.31) * mm, "end": v(2750.27, 2655.31) * mm});
            skLineSegment(sketch, "E83.top", {"start": v(2300.27, 4155.31) * mm, "end": v(2300.27, 2655.31) * mm});
            skLineSegment(sketch, "E83.left", {"start": v(2750.27, 4155.31) * mm, "end": v(2300.27, 4155.31) * mm});
            skLineSegment(sketch, "E83.right", {"start": v(2750.27, 2655.31) * mm, "end": v(2300.27, 2655.31) * mm});
            skPoint(sketch, "E83.middle", {"position": v(2525.27, 3405.31) * mm});
            skLineSegment(sketch, "E84.bottom", {"start": v(2750.27, 2637.83) * mm, "end": v(2750.27, 1137.83) * mm});
            skLineSegment(sketch, "E84.top", {"start": v(2300.27, 2637.83) * mm, "end": v(2300.27, 1137.83) * mm});
            skLineSegment(sketch, "E84.left", {"start": v(2750.27, 2637.83) * mm, "end": v(2300.27, 2637.83) * mm});
            skLineSegment(sketch, "E84.right", {"start": v(2750.27, 1137.83) * mm, "end": v(2300.27, 1137.83) * mm});
            skPoint(sketch, "E84.middle", {"position": v(2520.41, 1887.83) * mm});
            skLineSegment(sketch, "E85.bottom", {"start": v(2750.27, 1128.5) * mm, "end": v(2750.27, -371.5) * mm});
            skLineSegment(sketch, "E85.top", {"start": v(2300.27, 1128.5) * mm, "end": v(2300.27, -371.5) * mm});
            skLineSegment(sketch, "E85.left", {"start": v(2750.27, 1128.5) * mm, "end": v(2300.27, 1128.5) * mm});
            skLineSegment(sketch, "E85.right", {"start": v(2750.27, -371.5) * mm, "end": v(2300.27, -371.5) * mm});
            skPoint(sketch, "E85.middle", {"position": v(2525.27, 378.5) * mm});
            skLineSegment(sketch, "E86.bottom", {"start": v(1400.27, 1128.5) * mm, "end": v(1400.27, -371.5) * mm});
            skLineSegment(sketch, "E86.top", {"start": v(950.27, 1128.5) * mm, "end": v(950.27, -371.5) * mm});
            skLineSegment(sketch, "E86.left", {"start": v(1400.27, 1128.5) * mm, "end": v(950.27, 1128.5) * mm});
            skLineSegment(sketch, "E86.right", {"start": v(1400.27, -371.5) * mm, "end": v(950.27, -371.5) * mm});
            skPoint(sketch, "E86.middle", {"position": v(1175.27, 378.5) * mm});
            skLineSegment(sketch, "E87.bottom", {"start": v(1400.27, 2637.83) * mm, "end": v(1400.27, 1137.83) * mm});
            skLineSegment(sketch, "E87.top", {"start": v(950.27, 2637.83) * mm, "end": v(950.27, 1137.83) * mm});
            skLineSegment(sketch, "E87.left", {"start": v(1400.27, 2637.83) * mm, "end": v(950.27, 2637.83) * mm});
            skLineSegment(sketch, "E87.right", {"start": v(1400.27, 1137.83) * mm, "end": v(950.27, 1137.83) * mm});
            skPoint(sketch, "E87.middle", {"position": v(1175.27, 1887.83) * mm});
            skLineSegment(sketch, "E88.bottom", {"start": v(1526.7, 8477.17) * mm, "end": v(1526.7, 6977.17) * mm});
            skLineSegment(sketch, "E88.top", {"start": v(906.7, 8477.17) * mm, "end": v(906.7, 6977.17) * mm});
            skLineSegment(sketch, "E88.left", {"start": v(1526.7, 8477.17) * mm, "end": v(906.7, 8477.17) * mm});
            skPoint(sketch, "E88.middle", {"position": v(1216.7, 7727.17) * mm});
            skLineSegment(sketch, "E89", {"start": v(1526.7, 6977.17) * mm, "end": v(906.7, 6977.17) * mm});
            skLineSegment(sketch, "E90.bottom", {"start": v(1521.26, 6941.02) * mm, "end": v(1521.26, 5441.02) * mm});
            skLineSegment(sketch, "E90.top", {"start": v(901.26, 6941.02) * mm, "end": v(901.26, 5441.02) * mm});
            skLineSegment(sketch, "E90.left", {"start": v(1521.26, 6941.02) * mm, "end": v(901.26, 6941.02) * mm});
            skPoint(sketch, "E90.middle", {"position": v(1211.26, 6191.02) * mm});
            skLineSegment(sketch, "E91", {"start": v(1521.26, 5441.02) * mm, "end": v(901.26, 5441.02) * mm});
            skLineSegment(sketch, "E92.bottom", {"start": v(5025.03, -2298.58) * mm, "end": v(5775.03, -2298.58) * mm});
            skLineSegment(sketch, "E92.top", {"start": v(5025.03, -3048.58) * mm, "end": v(5775.03, -3048.58) * mm});
            skLineSegment(sketch, "E92.left", {"start": v(5025.03, -2298.58) * mm, "end": v(5025.03, -3048.58) * mm});
            skLineSegment(sketch, "E92.right", {"start": v(5775.03, -2298.58) * mm, "end": v(5775.03, -3048.58) * mm});
            skLineSegment(sketch, "E93.bottom", {"start": v(30, -7895) * mm, "end": v(930, -7895) * mm});
            skLineSegment(sketch, "E93.top", {"start": v(30, -8495) * mm, "end": v(930, -8495) * mm});
            skLineSegment(sketch, "E93.left", {"start": v(30, -7895) * mm, "end": v(30, -8495) * mm});
            skLineSegment(sketch, "E93.right", {"start": v(930, -7895) * mm, "end": v(930, -8495) * mm});
            skLineSegment(sketch, "E94.bottom", {"start": v(76.53, -7825) * mm, "end": v(76.53, -6325) * mm});
            skLineSegment(sketch, "E94.top", {"start": v(526.53, -7825) * mm, "end": v(526.53, -6325) * mm});
            skLineSegment(sketch, "E94.left", {"start": v(76.53, -7825) * mm, "end": v(526.53, -7825) * mm});
            skLineSegment(sketch, "E94.right", {"start": v(76.53, -6325) * mm, "end": v(526.53, -6325) * mm});
            skLineSegment(sketch, "E95.bottom", {"start": v(76.53, -6276.16) * mm, "end": v(76.53, -4776.16) * mm});
            skLineSegment(sketch, "E95.top", {"start": v(526.53, -6276.16) * mm, "end": v(526.53, -4776.16) * mm});
            skLineSegment(sketch, "E95.left", {"start": v(76.53, -6276.16) * mm, "end": v(526.53, -6276.16) * mm});
            skLineSegment(sketch, "E95.right", {"start": v(76.53, -4776.16) * mm, "end": v(526.53, -4776.16) * mm});
            skLineSegment(sketch, "E96.bottom", {"start": v(76.53, -1019.37) * mm, "end": v(826.53, -1019.37) * mm});
            skLineSegment(sketch, "E96.top", {"start": v(76.53, -1769.37) * mm, "end": v(826.53, -1769.37) * mm});
            skLineSegment(sketch, "E96.left", {"start": v(76.53, -1019.37) * mm, "end": v(76.53, -1769.37) * mm});
            skLineSegment(sketch, "E96.right", {"start": v(826.53, -1019.37) * mm, "end": v(826.53, -1769.37) * mm});
            skLineSegment(sketch, "E97.bottom", {"start": v(2424.2, -1019.37) * mm, "end": v(2424.2, -1819.37) * mm});
            skLineSegment(sketch, "E97.top", {"start": v(924.2, -1019.37) * mm, "end": v(924.2, -1819.37) * mm});
            skLineSegment(sketch, "E97.left", {"start": v(2424.2, -1019.37) * mm, "end": v(924.2, -1019.37) * mm});
            skLineSegment(sketch, "E97.right", {"start": v(2424.2, -1819.37) * mm, "end": v(924.2, -1819.37) * mm});
            skLineSegment(sketch, "E98.bottom", {"start": v(2491.14, -1019.37) * mm, "end": v(3991.14, -1019.37) * mm});
            skLineSegment(sketch, "E98.top", {"start": v(2491.14, -1469.37) * mm, "end": v(3991.14, -1469.37) * mm});
            skLineSegment(sketch, "E98.left", {"start": v(2491.14, -1019.37) * mm, "end": v(2491.14, -1469.37) * mm});
            skLineSegment(sketch, "E98.right", {"start": v(3991.14, -1019.37) * mm, "end": v(3991.14, -1469.37) * mm});
            skLineSegment(sketch, "E99.bottom", {"start": v(4021.14, -1019.37) * mm, "end": v(5521.14, -1019.37) * mm});
            skLineSegment(sketch, "E99.top", {"start": v(4021.14, -1469.37) * mm, "end": v(5521.14, -1469.37) * mm});
            skLineSegment(sketch, "E99.left", {"start": v(4021.14, -1019.37) * mm, "end": v(4021.14, -1469.37) * mm});
            skLineSegment(sketch, "E99.right", {"start": v(5521.14, -1019.37) * mm, "end": v(5521.14, -1469.37) * mm});
            skLineSegment(sketch, "E100.bottom", {"start": v(1787.35, -2748.15) * mm, "end": v(2537.35, -2748.15) * mm});
            skLineSegment(sketch, "E100.top", {"start": v(1787.35, -3498.15) * mm, "end": v(2537.35, -3498.15) * mm});
            skLineSegment(sketch, "E100.left", {"start": v(1787.35, -2748.15) * mm, "end": v(1787.35, -3498.15) * mm});
            skLineSegment(sketch, "E100.right", {"start": v(2537.35, -2748.15) * mm, "end": v(2537.35, -3498.15) * mm});
            skLineSegment(sketch, "E101.bottom", {"start": v(1737.35, -3548.58) * mm, "end": v(2537.35, -3548.58) * mm});
            skLineSegment(sketch, "E101.top", {"start": v(1737.35, -5048.58) * mm, "end": v(2537.35, -5048.58) * mm});
            skLineSegment(sketch, "E101.left", {"start": v(1737.35, -3548.58) * mm, "end": v(1737.35, -5048.58) * mm});
            skLineSegment(sketch, "E101.right", {"start": v(2537.35, -3548.58) * mm, "end": v(2537.35, -5048.58) * mm});
            skLineSegment(sketch, "E102.bottom", {"start": v(2099.98, -8187) * mm, "end": v(2099.98, -6687) * mm});
            skLineSegment(sketch, "E102.top", {"start": v(2549.98, -8187) * mm, "end": v(2549.98, -6687) * mm});
            skLineSegment(sketch, "E102.left", {"start": v(2099.98, -8187) * mm, "end": v(2549.98, -8187) * mm});
            skLineSegment(sketch, "E102.right", {"start": v(2099.98, -6687) * mm, "end": v(2549.98, -6687) * mm});
            skLineSegment(sketch, "E103.bottom", {"start": v(2092.87, -6621.47) * mm, "end": v(2092.87, -5121.47) * mm});
            skLineSegment(sketch, "E103.top", {"start": v(2542.87, -6621.47) * mm, "end": v(2542.87, -5121.47) * mm});
            skLineSegment(sketch, "E103.left", {"start": v(2092.87, -6621.47) * mm, "end": v(2542.87, -6621.47) * mm});
            skLineSegment(sketch, "E103.right", {"start": v(2092.87, -5121.47) * mm, "end": v(2542.87, -5121.47) * mm});
            skLineSegment(sketch, "E104.bottom", {"start": v(2589.98, -7895) * mm, "end": v(3489.98, -7895) * mm});
            skLineSegment(sketch, "E104.top", {"start": v(2589.98, -8495) * mm, "end": v(3489.98, -8495) * mm});
            skLineSegment(sketch, "E104.left", {"start": v(2589.98, -7895) * mm, "end": v(2589.98, -8495) * mm});
            skLineSegment(sketch, "E104.right", {"start": v(3489.98, -7895) * mm, "end": v(3489.98, -8495) * mm});
            skLineSegment(sketch, "E105.bottom", {"start": v(2589.98, -5426.16) * mm, "end": v(3339.98, -5426.16) * mm});
            skLineSegment(sketch, "E105.top", {"start": v(2589.98, -6176.16) * mm, "end": v(3339.98, -6176.16) * mm});
            skLineSegment(sketch, "E105.left", {"start": v(2589.98, -5426.16) * mm, "end": v(2589.98, -6176.16) * mm});
            skLineSegment(sketch, "E105.right", {"start": v(3339.98, -5426.16) * mm, "end": v(3339.98, -6176.16) * mm});
            skLineSegment(sketch, "E106.bottom", {"start": v(5040.1, -1663) * mm, "end": v(5540.1, -1663) * mm});
            skLineSegment(sketch, "E106.top", {"start": v(5040.1, -2163) * mm, "end": v(5540.1, -2163) * mm});
            skLineSegment(sketch, "E106.left", {"start": v(5040.1, -1663) * mm, "end": v(5040.1, -2163) * mm});
            skLineSegment(sketch, "E106.right", {"start": v(5540.1, -1663) * mm, "end": v(5540.1, -2163) * mm});
            skLineSegment(sketch, "E107.bottom", {"start": v(2715.73, -4861.47) * mm, "end": v(3215.73, -4861.47) * mm});
            skLineSegment(sketch, "E107.top", {"start": v(2715.73, -5361.47) * mm, "end": v(3215.73, -5361.47) * mm});
            skLineSegment(sketch, "E107.left", {"start": v(2715.73, -4861.47) * mm, "end": v(2715.73, -5361.47) * mm});
            skLineSegment(sketch, "E107.right", {"start": v(3215.73, -4861.47) * mm, "end": v(3215.73, -5361.47) * mm});
            skLineSegment(sketch, "E108.bottom", {"start": v(2589.98, -2798.58) * mm, "end": v(3339.98, -2798.58) * mm});
            skLineSegment(sketch, "E108.top", {"start": v(2589.98, -3498.15) * mm, "end": v(3339.98, -3498.15) * mm});
            skLineSegment(sketch, "E108.left", {"start": v(2589.98, -2748.15) * mm, "end": v(2589.98, -3498.15) * mm});
            skLineSegment(sketch, "E108.right", {"start": v(3339.98, -2748.15) * mm, "end": v(3339.98, -3498.15) * mm});
            skLineSegment(sketch, "E109.bottom", {"start": v(2589.98, -6245) * mm, "end": v(3389.98, -6245) * mm});
            skLineSegment(sketch, "E109.top", {"start": v(2589.98, -7745) * mm, "end": v(3389.98, -7745) * mm});
            skLineSegment(sketch, "E109.left", {"start": v(2589.98, -6245) * mm, "end": v(2589.98, -7745) * mm});
            skLineSegment(sketch, "E109.right", {"start": v(3389.98, -6245) * mm, "end": v(3389.98, -7745) * mm});
            skLineSegment(sketch, "E110.bottom", {"start": v(3225.45, -3797.34) * mm, "end": v(3225.45, -4697.34) * mm});
            skLineSegment(sketch, "E110.top", {"start": v(2625.45, -3797.34) * mm, "end": v(2625.45, -4697.34) * mm});
            skLineSegment(sketch, "E110.left", {"start": v(3225.45, -3797.34) * mm, "end": v(2625.45, -3797.34) * mm});
            skLineSegment(sketch, "E110.right", {"start": v(3225.45, -4697.34) * mm, "end": v(2625.45, -4697.34) * mm});
            skLineSegment(sketch, "E111.bottom", {"start": v(3935.03, -1683) * mm, "end": v(4835.03, -1683) * mm});
            skLineSegment(sketch, "E111.top", {"start": v(3935.03, -2283) * mm, "end": v(4835.03, -2283) * mm});
            skLineSegment(sketch, "E111.left", {"start": v(3935.03, -1683) * mm, "end": v(3935.03, -2283) * mm});
            skLineSegment(sketch, "E111.right", {"start": v(4835.03, -1683) * mm, "end": v(4835.03, -2283) * mm});
            skLineSegment(sketch, "E112.bottom", {"start": v(4099.25, -2448.14) * mm, "end": v(4849.25, -2448.14) * mm});
            skLineSegment(sketch, "E112.top", {"start": v(4099.25, -3198.14) * mm, "end": v(4849.25, -3198.14) * mm});
            skLineSegment(sketch, "E112.left", {"start": v(4099.25, -2448.14) * mm, "end": v(4099.25, -3198.14) * mm});
            skLineSegment(sketch, "E112.right", {"start": v(4849.25, -2448.14) * mm, "end": v(4849.25, -3198.14) * mm});
            skLineSegment(sketch, "E113.bottom", {"start": v(4021.25, -3548.58) * mm, "end": v(4821.25, -3548.58) * mm});
            skLineSegment(sketch, "E113.top", {"start": v(4021.25, -5048.58) * mm, "end": v(4821.25, -5048.58) * mm});
            skLineSegment(sketch, "E113.left", {"start": v(4021.25, -3548.58) * mm, "end": v(4021.25, -5048.58) * mm});
            skLineSegment(sketch, "E113.right", {"start": v(4821.25, -3548.58) * mm, "end": v(4821.25, -5048.58) * mm});
            skLineSegment(sketch, "E114.bottom", {"start": v(4380.02, -8187) * mm, "end": v(4380.02, -6687) * mm});
            skLineSegment(sketch, "E114.top", {"start": v(4830.02, -8187) * mm, "end": v(4830.02, -6687) * mm});
            skLineSegment(sketch, "E114.left", {"start": v(4380.02, -8187) * mm, "end": v(4830.02, -8187) * mm});
            skLineSegment(sketch, "E114.right", {"start": v(4380.02, -6687) * mm, "end": v(4830.02, -6687) * mm});
            skLineSegment(sketch, "E115.bottom", {"start": v(4356.8, -6603.54) * mm, "end": v(4356.8, -5103.54) * mm});
            skLineSegment(sketch, "E115.top", {"start": v(4806.8, -6603.54) * mm, "end": v(4806.8, -5103.54) * mm});
            skLineSegment(sketch, "E115.left", {"start": v(4356.8, -6603.54) * mm, "end": v(4806.8, -6603.54) * mm});
            skLineSegment(sketch, "E115.right", {"start": v(4356.8, -5103.54) * mm, "end": v(4806.8, -5103.54) * mm});
            skLineSegment(sketch, "E116.bottom", {"start": v(4954.69, -4598.1) * mm, "end": v(4954.69, -3098.1) * mm});
            skLineSegment(sketch, "E116.top", {"start": v(5404.69, -4598.1) * mm, "end": v(5404.69, -3098.1) * mm});
            skLineSegment(sketch, "E116.left", {"start": v(4954.69, -4598.1) * mm, "end": v(5404.69, -4598.1) * mm});
            skLineSegment(sketch, "E116.right", {"start": v(4954.69, -3098.1) * mm, "end": v(5404.69, -3098.1) * mm});
            skLineSegment(sketch, "E117.bottom", {"start": v(4954.69, -6237.65) * mm, "end": v(4954.69, -4737.65) * mm});
            skLineSegment(sketch, "E117.top", {"start": v(5404.69, -6237.65) * mm, "end": v(5404.69, -4737.65) * mm});
            skLineSegment(sketch, "E117.left", {"start": v(4954.69, -6237.65) * mm, "end": v(5404.69, -6237.65) * mm});
            skLineSegment(sketch, "E117.right", {"start": v(4954.69, -4737.65) * mm, "end": v(5404.69, -4737.65) * mm});
            skLineSegment(sketch, "E118.bottom", {"start": v(4937.88, -7785) * mm, "end": v(4937.88, -6285) * mm});
            skLineSegment(sketch, "E118.top", {"start": v(5387.88, -7785) * mm, "end": v(5387.88, -6285) * mm});
            skLineSegment(sketch, "E118.left", {"start": v(4937.88, -7785) * mm, "end": v(5387.88, -7785) * mm});
            skLineSegment(sketch, "E118.right", {"start": v(4937.88, -6285) * mm, "end": v(5387.88, -6285) * mm});
            skLineSegment(sketch, "E119.bottom", {"start": v(4937.88, -7895) * mm, "end": v(5837.88, -7895) * mm});
            skLineSegment(sketch, "E119.top", {"start": v(4937.88, -8495) * mm, "end": v(5837.88, -8495) * mm});
            skLineSegment(sketch, "E119.left", {"start": v(4937.88, -7895) * mm, "end": v(4937.88, -8495) * mm});
            skLineSegment(sketch, "E119.right", {"start": v(5837.88, -7895) * mm, "end": v(5837.88, -8495) * mm});
            skLineSegment(sketch, "E120.bottom", {"start": v(6737.4, -6678.23) * mm, "end": v(7537.4, -6678.23) * mm});
            skLineSegment(sketch, "E120.top", {"start": v(6737.4, -8178.23) * mm, "end": v(7537.4, -8178.23) * mm});
            skLineSegment(sketch, "E120.left", {"start": v(6737.4, -6678.23) * mm, "end": v(6737.4, -8178.23) * mm});
            skLineSegment(sketch, "E120.right", {"start": v(7537.4, -6678.23) * mm, "end": v(7537.4, -8178.23) * mm});
            skLineSegment(sketch, "E121.bottom", {"start": v(6737.4, -5103.54) * mm, "end": v(7537.4, -5103.54) * mm});
            skLineSegment(sketch, "E121.top", {"start": v(6737.4, -6603.54) * mm, "end": v(7537.4, -6603.54) * mm});
            skLineSegment(sketch, "E121.left", {"start": v(6737.4, -5103.54) * mm, "end": v(6737.4, -6603.54) * mm});
            skLineSegment(sketch, "E121.right", {"start": v(7537.4, -5103.54) * mm, "end": v(7537.4, -6603.54) * mm});
            skLineSegment(sketch, "E122.bottom", {"start": v(9391.63, -8030.62) * mm, "end": v(9391.63, -6530.62) * mm});
            skLineSegment(sketch, "E122.top", {"start": v(9841.63, -8030.62) * mm, "end": v(9841.63, -6530.62) * mm});
            skLineSegment(sketch, "E122.left", {"start": v(9391.63, -8030.62) * mm, "end": v(9841.63, -8030.62) * mm});
            skLineSegment(sketch, "E122.right", {"start": v(9391.63, -6530.62) * mm, "end": v(9841.63, -6530.62) * mm});
            skLineSegment(sketch, "E123.bottom", {"start": v(9414.44, -6498.29) * mm, "end": v(9414.44, -4998.29) * mm});
            skLineSegment(sketch, "E123.top", {"start": v(9864.44, -6498.29) * mm, "end": v(9864.44, -4998.29) * mm});
            skLineSegment(sketch, "E123.left", {"start": v(9414.44, -6498.29) * mm, "end": v(9864.44, -6498.29) * mm});
            skLineSegment(sketch, "E123.right", {"start": v(9414.44, -4998.29) * mm, "end": v(9864.44, -4998.29) * mm});
            skLineSegment(sketch, "E124.bottom", {"start": v(7577.4, -7428.23) * mm, "end": v(8327.4, -7428.23) * mm});
            skLineSegment(sketch, "E124.top", {"start": v(7577.4, -8178.23) * mm, "end": v(8327.4, -8178.23) * mm});
            skLineSegment(sketch, "E124.left", {"start": v(7577.4, -7428.23) * mm, "end": v(7577.4, -8178.23) * mm});
            skLineSegment(sketch, "E124.right", {"start": v(8327.4, -7428.23) * mm, "end": v(8327.4, -8178.23) * mm});
            skLineSegment(sketch, "E125.bottom", {"start": v(7577.4, -6650.63) * mm, "end": v(8327.4, -6650.63) * mm});
            skLineSegment(sketch, "E125.top", {"start": v(7577.4, -7400.63) * mm, "end": v(8327.4, -7400.63) * mm});
            skLineSegment(sketch, "E125.left", {"start": v(7577.4, -6650.63) * mm, "end": v(7577.4, -7400.63) * mm});
            skLineSegment(sketch, "E125.right", {"start": v(8327.4, -6650.63) * mm, "end": v(8327.4, -7400.63) * mm});
            skLineSegment(sketch, "E126.bottom", {"start": v(7587.14, -5103.54) * mm, "end": v(8387.14, -5103.54) * mm});
            skLineSegment(sketch, "E126.top", {"start": v(7587.14, -6603.54) * mm, "end": v(8387.14, -6603.54) * mm});
            skLineSegment(sketch, "E126.left", {"start": v(7587.14, -5103.54) * mm, "end": v(7587.14, -6603.54) * mm});
            skLineSegment(sketch, "E126.right", {"start": v(8387.14, -5103.54) * mm, "end": v(8387.14, -6603.54) * mm});
            skLineSegment(sketch, "E127.bottom", {"start": v(9188.03, -8098.25) * mm, "end": v(9888.03, -8098.25) * mm});
            skLineSegment(sketch, "E127.top", {"start": v(9188.03, -8498.25) * mm, "end": v(9888.03, -8498.25) * mm});
            skLineSegment(sketch, "E127.left", {"start": v(9188.03, -8098.25) * mm, "end": v(9188.03, -8498.25) * mm});
            skLineSegment(sketch, "E127.right", {"start": v(9888.03, -8098.25) * mm, "end": v(9888.03, -8498.25) * mm});
            skLineSegment(sketch, "E128.bottom", {"start": v(9841.63, -2141.79) * mm, "end": v(8341.63, -2141.79) * mm});
            skLineSegment(sketch, "E128.top", {"start": v(9841.63, -1691.79) * mm, "end": v(8341.63, -1691.79) * mm});
            skLineSegment(sketch, "E128.left", {"start": v(9841.63, -2141.79) * mm, "end": v(9841.63, -1691.79) * mm});
            skLineSegment(sketch, "E128.right", {"start": v(8341.63, -2141.79) * mm, "end": v(8341.63, -1691.79) * mm});
            skLineSegment(sketch, "E129.bottom", {"start": v(8237.4, -2141.79) * mm, "end": v(6737.4, -2141.79) * mm});
            skLineSegment(sketch, "E129.top", {"start": v(8237.4, -1691.79) * mm, "end": v(6737.4, -1691.79) * mm});
            skLineSegment(sketch, "E129.left", {"start": v(8237.4, -2141.79) * mm, "end": v(8237.4, -1691.79) * mm});
            skLineSegment(sketch, "E129.right", {"start": v(6737.4, -2141.79) * mm, "end": v(6737.4, -1691.79) * mm});
            skLineSegment(sketch, "E130.bottom", {"start": v(9841.63, -3183.43) * mm, "end": v(8341.63, -3183.43) * mm});
            skLineSegment(sketch, "E130.top", {"start": v(9841.63, -2733.43) * mm, "end": v(8341.63, -2733.43) * mm});
            skLineSegment(sketch, "E130.left", {"start": v(9841.63, -3183.43) * mm, "end": v(9841.63, -2733.43) * mm});
            skLineSegment(sketch, "E130.right", {"start": v(8341.63, -3183.43) * mm, "end": v(8341.63, -2733.43) * mm});
            skLineSegment(sketch, "E131.bottom", {"start": v(8237.4, -3183.43) * mm, "end": v(6737.4, -3183.43) * mm});
            skLineSegment(sketch, "E131.top", {"start": v(8237.4, -2733.43) * mm, "end": v(6737.4, -2733.43) * mm});
            skLineSegment(sketch, "E131.left", {"start": v(8237.4, -3183.43) * mm, "end": v(8237.4, -2733.43) * mm});
            skLineSegment(sketch, "E131.right", {"start": v(6737.4, -3183.43) * mm, "end": v(6737.4, -2733.43) * mm});
            skLineSegment(sketch, "E132.bottom", {"start": v(9887.14, -4221.52) * mm, "end": v(8387.14, -4221.52) * mm});
            skLineSegment(sketch, "E132.top", {"start": v(9887.14, -3771.52) * mm, "end": v(8387.14, -3771.52) * mm});
            skLineSegment(sketch, "E132.left", {"start": v(9887.14, -4221.52) * mm, "end": v(9887.14, -3771.52) * mm});
            skLineSegment(sketch, "E132.right", {"start": v(8387.14, -4221.52) * mm, "end": v(8387.14, -3771.52) * mm});
            skLineSegment(sketch, "E133.bottom", {"start": v(8237.4, -4221) * mm, "end": v(6737.4, -4221) * mm});
            skLineSegment(sketch, "E133.top", {"start": v(8237.4, -3771) * mm, "end": v(6737.4, -3771) * mm});
            skLineSegment(sketch, "E133.left", {"start": v(8237.4, -4221) * mm, "end": v(8237.4, -3771) * mm});
            skLineSegment(sketch, "E133.right", {"start": v(6737.4, -4221) * mm, "end": v(6737.4, -3771) * mm});
            skLineSegment(sketch, "E134.bottom", {"start": v(79.53, -4297.34) * mm, "end": v(779.53, -4297.34) * mm});
            skLineSegment(sketch, "E134.top", {"start": v(79.53, -4697.34) * mm, "end": v(779.53, -4697.34) * mm});
            skLineSegment(sketch, "E134.left", {"start": v(79.53, -4297.34) * mm, "end": v(79.53, -4697.34) * mm});
            skLineSegment(sketch, "E134.right", {"start": v(779.53, -4297.34) * mm, "end": v(779.53, -4697.34) * mm});
            skLineSegment(sketch, "E135.bottom", {"start": v(85, -2706.35) * mm, "end": v(885, -2706.35) * mm});
            skLineSegment(sketch, "E135.top", {"start": v(85, -4206.35) * mm, "end": v(885, -4206.35) * mm});
            skLineSegment(sketch, "E135.left", {"start": v(85, -2706.35) * mm, "end": v(85, -4206.35) * mm});
            skLineSegment(sketch, "E135.right", {"start": v(885, -2706.35) * mm, "end": v(885, -4206.35) * mm});
            skSolve(sketch);
        }
        {
            var Q0;
            Q0 = qSketchRegion(id + "F4", true);
            extrude(context, id + "F5", {"entities" : qUnion([Q0]), "depth" : 25 * mm});
        }
    });
